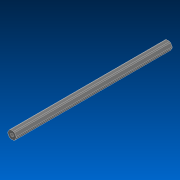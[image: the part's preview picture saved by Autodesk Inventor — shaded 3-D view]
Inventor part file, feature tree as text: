
AUTODESK INVENTOR PART (.ipt)
format: ipt  version: 2022.2 (Build 262287000, 287)  size: 121,344 bytes
history: native  units: in
note: dims shown in document units (in); Inventor stores cm internally (conversion verified against a paired STEP export)
features: extrude x1, sketch x1, other x1
ambient origin geometry x8: Origin, YZ Plane, XZ Plane, XY Plane, X Axis, Y Axis, Z Axis, Center Point
bodies: Solid1 (feature_tree)
feature tree (3):
  extrude  "Extrusion1"  TaperAngle=0.0deg  [1 undecoded]
  sketch  "Sketch1"  dims[d0=26.0in d1=0.0in]
  other  "Cut-Extrude2"
note: 1 required parameter value undecoded (feature->parameter linkage not recoverable at this tier; creation-order binding heuristic only, values carry confidence <= 0.55)
